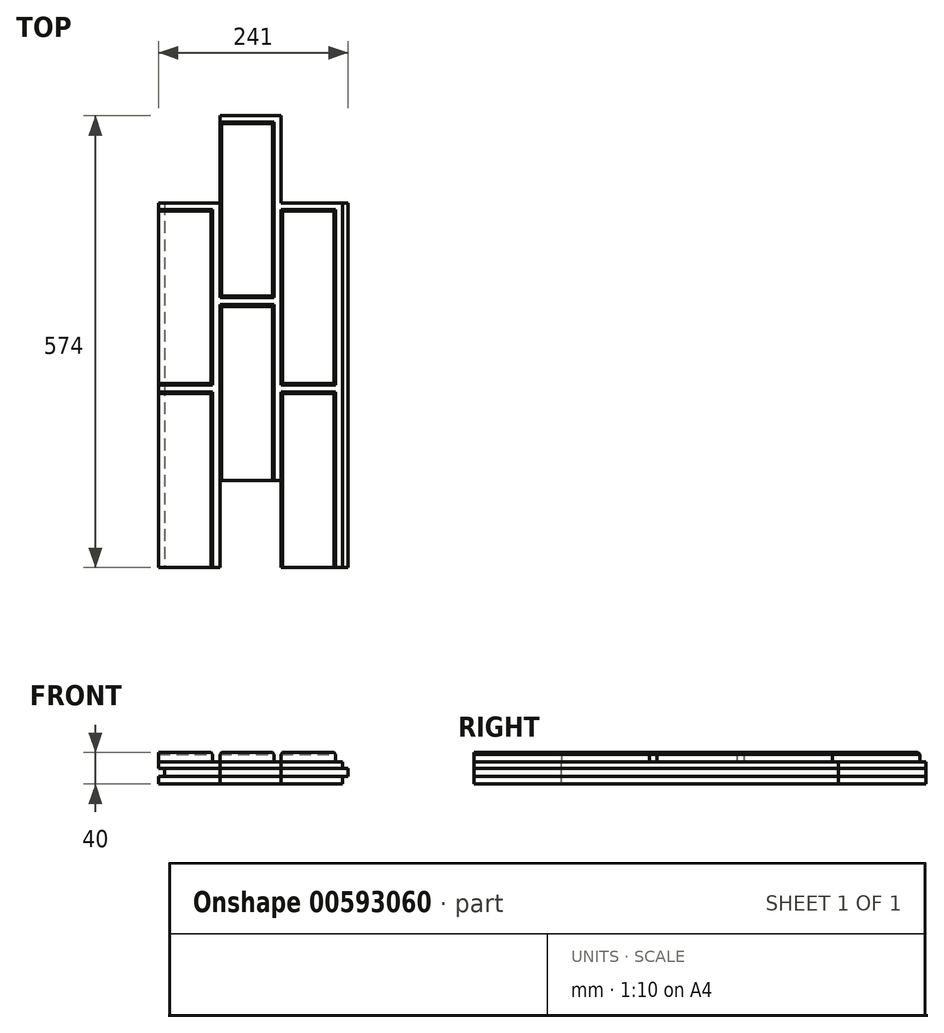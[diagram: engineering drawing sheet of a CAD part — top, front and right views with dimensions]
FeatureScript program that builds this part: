
annotation { "Feature Type Name" : "Feature", "Feature Type Description" : "" }
export const myFeature = defineFeature(function(context is Context, id is Id, definition is map)
    precondition{}
    {
        {
            var Q0;
            Q0=qCreatedBy(makeId("Front.planeOp"),FACE);
            var sketch = newSketch(context, id + "F0", { "sketchPlane" : qUnion([Q0])});
            skLineSegment(sketch, "E0.bottom", {"start": v(117, 0) * mm, "end": v(-117, 0) * mm});
            skLineSegment(sketch, "E0.top", {"start": v(117, 10) * mm, "end": v(-117, 10) * mm});
            skLineSegment(sketch, "E0.left", {"start": v(117, 0) * mm, "end": v(117, 10) * mm});
            skLineSegment(sketch, "E0.right", {"start": v(-117, 0) * mm, "end": v(-117, 10) * mm});
            skPoint(sketch, "E0.middle", {"position": v(0, 5) * mm});
            skSolve(sketch);
        }
        {
            var Q0;
            Q0 = qSketchRegion(id + "F0", true);
            extrude(context, id + "F1", {"entities" : qUnion([Q0]), "depth" : ((((222 + 10) * 2) / 2) + (111 / 2)) * mm, "offsetDistance" : 25 * mm, "hasSecondDirection" : true, "secondDirectionOppositeDirection" : true, "secondDirectionDepth" : ((((222 + 10) * 2) / 2) + (111 / 2)) * mm});
        }
        {
            var Q0;
            Q0=makeQuery(id+"F1.opExtrude","CAP_FACE",FACE,{"disambiguationData":[OSD([sQuery(id+"F0.wireOp",EDGE,"E0.bottom"),sQuery(id+"F0.wireOp",EDGE,"E0.top"),sQuery(id+"F0.wireOp",EDGE,"E0.left"),sQuery(id+"F0.wireOp",EDGE,"E0.right")])],"isStart":false});
            var sketch = newSketch(context, id + "F2", { "sketchPlane" : qUnion([Q0])});
            skLineSegment(sketch, "E1.bottom", {"start": v(-109, 10) * mm, "end": v(124, 10) * mm});
            skLineSegment(sketch, "E1.top", {"start": v(-109, 20) * mm, "end": v(124, 20) * mm});
            skLineSegment(sketch, "E1.left", {"start": v(-109, 10) * mm, "end": v(-109, 20) * mm});
            skLineSegment(sketch, "E1.right", {"start": v(124, 10) * mm, "end": v(124, 20) * mm});
            skSolve(sketch);
        }
        {
            var Q0;
            Q0 = qSketchRegion(id + "F2", true);
            var Q1;
            Q1=makeQuery(id+"F1.opExtrude","CAP_FACE",FACE,{"disambiguationData":[OSD([sQuery(id+"F0.wireOp",EDGE,"E0.bottom"),sQuery(id+"F0.wireOp",EDGE,"E0.top"),sQuery(id+"F0.wireOp",EDGE,"E0.left"),sQuery(id+"F0.wireOp",EDGE,"E0.right")])],"isStart":true});
            extrude(context, id + "F3", {"entities" : qUnion([Q0]), "endBound" : BoundingType.UP_TO_SURFACE, "oppositeDirection" : true, "depth" : 25 * mm, "endBoundEntityFace" : qUnion([Q1]), "offsetDistance" : 25 * mm});
        }
        {
            var Q0;
            Q0=makeQuery(id+"F3.opExtrude","CAP_FACE",FACE,{"disambiguationData":[OSD([sQuery(id+"F2.wireOp",EDGE,"E1.bottom"),sQuery(id+"F2.wireOp",EDGE,"E1.top"),sQuery(id+"F2.wireOp",EDGE,"E1.left"),sQuery(id+"F2.wireOp",EDGE,"E1.right")])],"isStart":true});
            var sketch = newSketch(context, id + "F4", { "sketchPlane" : qUnion([Q0])});
            skLineSegment(sketch, "E2.0", {"start": v(117, 0) * mm, "end": v(117, 10) * mm, "construction": true});
            skLineSegment(sketch, "E3.0", {"start": v(117, 10) * mm, "end": v(-117, 10) * mm, "construction": true});
            skLineSegment(sketch, "E4.bottom", {"start": v(117, 20) * mm, "end": v(-117, 20) * mm});
            skLineSegment(sketch, "E4.top", {"start": v(117, 28) * mm, "end": v(-117, 28) * mm});
            skLineSegment(sketch, "E4.left", {"start": v(117, 20) * mm, "end": v(117, 28) * mm});
            skLineSegment(sketch, "E4.right", {"start": v(-117, 20) * mm, "end": v(-117, 28) * mm});
            skSolve(sketch);
        }
        {
            var Q0;
            Q0 = qSketchRegion(id + "F4", true);
            var Q1;
            Q1=makeQuery(id+"F3.opExtrude","CAP_FACE",FACE,{"disambiguationData":[OSD([sQuery(id+"F2.wireOp",EDGE,"E1.bottom"),sQuery(id+"F2.wireOp",EDGE,"E1.top"),sQuery(id+"F2.wireOp",EDGE,"E1.left"),sQuery(id+"F2.wireOp",EDGE,"E1.right")])],"isStart":false});
            extrude(context, id + "F5", {"entities" : qUnion([Q0]), "endBound" : BoundingType.UP_TO_SURFACE, "oppositeDirection" : true, "depth" : 25 * mm, "endBoundEntityFace" : qUnion([Q1]), "offsetDistance" : 25 * mm});
        }
        {
            var Q0;
            Q0=makeQuery(id+"F5.opExtrude","SWEPT_FACE",FACE,{"disambiguationData":[OSD([sQuery(id+"F4.wireOp",EDGE,"E4.top")])]});
            var sketch = newSketch(context, id + "F6", { "sketchPlane" : qUnion([Q0])});
            skLineSegment(sketch, "E5", {"start": v(-39, -287.5) * mm, "end": v(-39, 287.5) * mm, "construction": true});
            skLineSegment(sketch, "E6.bottom", {"start": v(-39, -287.5) * mm, "end": v(39, -287.5) * mm});
            skLineSegment(sketch, "E6.top", {"start": v(-39, -176.5) * mm, "end": v(39, -176.5) * mm});
            skLineSegment(sketch, "E6.left", {"start": v(-39, -287.5) * mm, "end": v(-39, -176.5) * mm});
            skLineSegment(sketch, "E6.right", {"start": v(39, -287.5) * mm, "end": v(39, -176.5) * mm});
            skLineSegment(sketch, "E7", {"start": v(39, -287.5) * mm, "end": v(39, 287.5) * mm, "construction": true});
            skLineSegment(sketch, "E8.bottom", {"start": v(-39, 176.5) * mm, "end": v(-117, 176.5) * mm});
            skLineSegment(sketch, "E8.top", {"start": v(-39, 287.5) * mm, "end": v(-117, 287.5) * mm});
            skLineSegment(sketch, "E8.left", {"start": v(-39, 176.5) * mm, "end": v(-39, 287.5) * mm});
            skLineSegment(sketch, "E8.right", {"start": v(-117, 176.5) * mm, "end": v(-117, 287.5) * mm});
            skLineSegment(sketch, "E9.0", {"start": v(124, 287.5) * mm, "end": v(124, -287.5) * mm, "construction": true});
            skLineSegment(sketch, "E10", {"start": v(-117, 176.5) * mm, "end": v(124, 176.5) * mm, "construction": true});
            skLineSegment(sketch, "E11.bottom", {"start": v(39, 176.5) * mm, "end": v(124, 176.5) * mm});
            skLineSegment(sketch, "E11.top", {"start": v(39, 287.5) * mm, "end": v(124, 287.5) * mm});
            skLineSegment(sketch, "E11.left", {"start": v(39, 176.5) * mm, "end": v(39, 287.5) * mm});
            skLineSegment(sketch, "E11.right", {"start": v(124, 176.5) * mm, "end": v(124, 287.5) * mm});
            skSolve(sketch);
        }
        {
            var Q0;
            Q0 = qSketchRegion(id + "F6", true);
            extrude(context, id + "F7", {"entities" : qUnion([Q0]), "operationType" : NewBodyOperationType.REMOVE, "endBound" : BoundingType.THROUGH_ALL, "oppositeDirection" : true, "depth" : 25 * mm, "offsetDistance" : 25 * mm});
        }
        {
            var Q0;
            Q0=makeQuery(id+"F5.opExtrude","SWEPT_FACE",FACE,{"disambiguationData":[OSD([sQuery(id+"F4.wireOp",EDGE,"E4.top")])]});
            var sketch = newSketch(context, id + "F8", { "sketchPlane" : qUnion([Q0])});
            skLineSegment(sketch, "E12.bottom", {"start": v(-117, -287.5) * mm, "end": v(-48, -287.5) * mm});
            skLineSegment(sketch, "E12.top", {"start": v(-117, -64.5) * mm, "end": v(-48, -64.5) * mm});
            skLineSegment(sketch, "E12.left", {"start": v(-117, -287.5) * mm, "end": v(-117, -64.5) * mm});
            skLineSegment(sketch, "E12.right", {"start": v(-48, -287.5) * mm, "end": v(-48, -64.5) * mm});
            skLineSegment(sketch, "E13.bottom", {"start": v(-117, -55.5) * mm, "end": v(-48, -55.5) * mm});
            skLineSegment(sketch, "E13.top", {"start": v(-117, 167.5) * mm, "end": v(-48, 167.5) * mm});
            skLineSegment(sketch, "E13.left", {"start": v(-117, -55.5) * mm, "end": v(-117, 167.5) * mm});
            skLineSegment(sketch, "E13.right", {"start": v(-48, -55.5) * mm, "end": v(-48, 167.5) * mm});
            skLineSegment(sketch, "E14.bottom", {"start": v(39, -287.5) * mm, "end": v(108, -287.5) * mm});
            skLineSegment(sketch, "E14.top", {"start": v(39, -64.5) * mm, "end": v(108, -64.5) * mm});
            skLineSegment(sketch, "E14.left", {"start": v(39, -287.5) * mm, "end": v(39, -64.5) * mm});
            skLineSegment(sketch, "E14.right", {"start": v(108, -287.5) * mm, "end": v(108, -64.5) * mm});
            skLineSegment(sketch, "E15.bottom", {"start": v(39, -55.5) * mm, "end": v(108, -55.5) * mm});
            skLineSegment(sketch, "E15.top", {"start": v(39, 167.5) * mm, "end": v(108, 167.5) * mm});
            skLineSegment(sketch, "E15.left", {"start": v(39, -55.5) * mm, "end": v(39, 167.5) * mm});
            skLineSegment(sketch, "E15.right", {"start": v(108, -55.5) * mm, "end": v(108, 167.5) * mm});
            skLineSegment(sketch, "E16.bottom", {"start": v(-39, -176.5) * mm, "end": v(30, -176.5) * mm});
            skLineSegment(sketch, "E16.top", {"start": v(-39, 46.5) * mm, "end": v(30, 46.5) * mm});
            skLineSegment(sketch, "E16.left", {"start": v(-39, -176.5) * mm, "end": v(-39, 46.5) * mm});
            skLineSegment(sketch, "E16.right", {"start": v(30, -176.5) * mm, "end": v(30, 46.5) * mm});
            skLineSegment(sketch, "E17.bottom", {"start": v(-39, 55.5) * mm, "end": v(30, 55.5) * mm});
            skLineSegment(sketch, "E17.top", {"start": v(-39, 278.5) * mm, "end": v(30, 278.5) * mm});
            skLineSegment(sketch, "E17.left", {"start": v(-39, 55.5) * mm, "end": v(-39, 278.5) * mm});
            skLineSegment(sketch, "E17.right", {"start": v(30, 55.5) * mm, "end": v(30, 278.5) * mm});
            skSolve(sketch);
        }
        {
            var Q0;
            Q0 = qSketchRegion(id + "F8", true);
            extrude(context, id + "F9", {"entities" : qUnion([Q0]), "depth" : 12 * mm, "offsetDistance" : 25 * mm});
        }
        {
            var Q0;
            Q0=makeQuery(id+"F9.opExtrude","CAP_EDGE",EDGE,{"disambiguationData":[OSD([sQuery(id+"F8.wireOp",EDGE,"E17.top")])],"isStart":false});
            var Q1;
            Q1=makeQuery(id+"F9.opExtrude","CAP_EDGE",EDGE,{"disambiguationData":[OSD([sQuery(id+"F8.wireOp",EDGE,"E17.right")])],"isStart":false});
            var Q2;
            Q2=makeQuery(id+"F9.opExtrude","CAP_EDGE",EDGE,{"disambiguationData":[OSD([sQuery(id+"F8.wireOp",EDGE,"E13.right")])],"isStart":false});
            var Q3;
            Q3=makeQuery(id+"F9.opExtrude","CAP_EDGE",EDGE,{"disambiguationData":[OSD([sQuery(id+"F8.wireOp",EDGE,"E13.top")])],"isStart":false});
            var Q4;
            Q4=makeQuery(id+"F9.opExtrude","CAP_EDGE",EDGE,{"disambiguationData":[OSD([sQuery(id+"F8.wireOp",EDGE,"E13.bottom")])],"isStart":false});
            var Q5;
            Q5=makeQuery(id+"F9.opExtrude","CAP_EDGE",EDGE,{"disambiguationData":[OSD([sQuery(id+"F8.wireOp",EDGE,"E12.top")])],"isStart":false});
            var Q6;
            Q6=makeQuery(id+"F9.opExtrude","CAP_EDGE",EDGE,{"disambiguationData":[OSD([sQuery(id+"F8.wireOp",EDGE,"E12.right")])],"isStart":false});
            var Q7;
            Q7=makeQuery(id+"F9.opExtrude","CAP_EDGE",EDGE,{"disambiguationData":[OSD([sQuery(id+"F8.wireOp",EDGE,"E17.bottom")])],"isStart":false});
            var Q8;
            Q8=makeQuery(id+"F9.opExtrude","CAP_EDGE",EDGE,{"disambiguationData":[OSD([sQuery(id+"F8.wireOp",EDGE,"E16.top")])],"isStart":false});
            var Q9;
            Q9=makeQuery(id+"F9.opExtrude","CAP_EDGE",EDGE,{"disambiguationData":[OSD([sQuery(id+"F8.wireOp",EDGE,"E16.left")])],"isStart":false});
            var Q10;
            Q10=makeQuery(id+"F9.opExtrude","CAP_EDGE",EDGE,{"disambiguationData":[OSD([sQuery(id+"F8.wireOp",EDGE,"E16.right")])],"isStart":false});
            var Q11;
            Q11=makeQuery(id+"F9.opExtrude","CAP_FACE",FACE,{"disambiguationData":[OSD([sQuery(id+"F8.wireOp",EDGE,"E15.bottom"),sQuery(id+"F8.wireOp",EDGE,"E15.top"),sQuery(id+"F8.wireOp",EDGE,"E15.left"),sQuery(id+"F8.wireOp",EDGE,"E15.right")])],"isStart":false});
            var Q12;
            Q12=makeQuery(id+"F9.opExtrude","CAP_EDGE",EDGE,{"disambiguationData":[OSD([sQuery(id+"F8.wireOp",EDGE,"E14.top")])],"isStart":false});
            var Q13;
            Q13=makeQuery(id+"F9.opExtrude","CAP_EDGE",EDGE,{"disambiguationData":[OSD([sQuery(id+"F8.wireOp",EDGE,"E14.right")])],"isStart":false});
            chamfer(context, id + "F10", {"entities" : qUnion([Q0, Q1, Q2, Q3, Q4, Q5, Q6, Q7, Q8, Q9, Q10, Q11, Q12, Q13]), "width" : 2 * mm, "tangentPropagation" : true});
        }
        {
            var Q0;
            Q0=makeQuery(id+"F9.opExtrude","CAP_EDGE",EDGE,{"disambiguationData":[OSD([sQuery(id+"F8.wireOp",EDGE,"E17.left")])],"isStart":false});
            var Q1;
            Q1=makeQuery(id+"F9.opExtrude","CAP_EDGE",EDGE,{"disambiguationData":[OSD([sQuery(id+"F8.wireOp",EDGE,"E14.left")])],"isStart":false});
            chamfer(context, id + "F11", {"entities" : qUnion([Q0, Q1]), "width" : 2 * mm, "tangentPropagation" : true});
        }
        {
            var Q0;
            Q0=makeQuery(id+"F1.opExtrude","SWEPT_FACE",FACE,{"disambiguationData":[OSD([sQuery(id+"F0.wireOp",EDGE,"E0.bottom")])]});
            var sketch = newSketch(context, id + "F12", { "sketchPlane" : qUnion([Q0])});
            skLineSegment(sketch, "E18.0", {"start": v(124, -176.5) * mm, "end": v(124, 287.5) * mm, "construction": true});
            skLineSegment(sketch, "E19", {"start": v(-117, -175.5) * mm, "end": v(-39, -175.5) * mm});
            skLineSegment(sketch, "E20", {"start": v(-39, -175.5) * mm, "end": v(-39, -176.5) * mm});
            skLineSegment(sketch, "E21", {"start": v(-39, -286.5) * mm, "end": v(39, -286.5) * mm});
            skLineSegment(sketch, "E22", {"start": v(39, -286.5) * mm, "end": v(39, -287.5) * mm});
            skLineSegment(sketch, "E23", {"start": v(39, -287.5) * mm, "end": v(-39, -287.5) * mm});
            skLineSegment(sketch, "E24", {"start": v(-39, -287.5) * mm, "end": v(-39, -286.5) * mm});
            skLineSegment(sketch, "E25", {"start": v(-117, -175.5) * mm, "end": v(-117, -176.5) * mm});
            skLineSegment(sketch, "E26", {"start": v(-117, -176.5) * mm, "end": v(-39, -176.5) * mm});
            skLineSegment(sketch, "E27", {"start": v(124, -176.5) * mm, "end": v(39, -176.5) * mm});
            skLineSegment(sketch, "E28", {"start": v(39, -176.5) * mm, "end": v(39, -175.5) * mm});
            skLineSegment(sketch, "E29", {"start": v(39, -175.5) * mm, "end": v(124, -175.5) * mm});
            skLineSegment(sketch, "E30", {"start": v(124, -175.5) * mm, "end": v(124, -176.5) * mm});
            skSolve(sketch);
        }
        {
            var Q0;
            Q0 = qSketchRegion(id + "F12", true);
            extrude(context, id + "F13", {"entities" : qUnion([Q0]), "operationType" : NewBodyOperationType.REMOVE, "endBound" : BoundingType.THROUGH_ALL, "oppositeDirection" : true, "depth" : 25 * mm, "offsetDistance" : 25 * mm});
        }
    });
